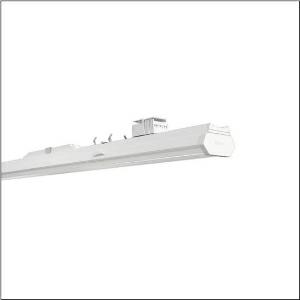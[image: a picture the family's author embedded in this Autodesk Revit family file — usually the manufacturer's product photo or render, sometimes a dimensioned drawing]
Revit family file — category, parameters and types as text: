
# Revit family: licross_r__21_protected_mo_52td12dn4a5g3s4_b622
name_source: partatom
category: Lighting Fixtures
units: mm (PartAtom-declared; Revit-internal decimal feet)

## family parameters
Cut with Voids When Loaded = No
Host = Face
Light Source = No
Part Type = Normal
Room Calculation Point = No
Round Connector Dimension = Use Diameter
Shared = No

## types (1)
- --- (1 x LED, 940 lm, 6.8 W, 4000K)
    Apparent Load = 7 VA
    CIE Flux Codes = 73 92 98 99 100
    Color Rendering = 80
    Color Temperature = 4000K
    Default Elevation = 1800 mm
    Description = Licross® 21 Protected MO, luminaire insert, of sheet steel, galvanised, coil coated, white, length: 1.500mm, width: 90mm, height: 103mm, LED rated luminous flux: 10.700lm, light colour: 840, control gear: DALI 2, with plug, 6-pole, with phase selection, for trunking rail, 9 or 11-core, mains connection: 220..240V, AC, 50/60Hz, rated input power: 66W, for trunking rail, 9-/11-core, internal wiring halogen-free, for emergency light function, converter,control gear: single battery element, battery: LiFePO4, 9Ah, primary light control with lens, of plastic, primary optical cover: cover, of PMMA, light emission: direct distribution, primary light characteristic: symmetric, protection rating (complete): IP54, insulation class (complete): insulation class I (protective earthing), certification: CE, UKCA, protection symbol: D if used in an environment with non-conductive dust loads with corresponding accessories, impact resistance: IK06, permissible ambient temperature for indoor applications: +5..+35°C, standard: EN 60598-2-22, LABS conformity tested according to VDMA 24364:2018-05, reducing of maximum allowable ambient temperature of 5°C with ceiling mounting, corresponds to IFS (International Featured Standards) requirements for safety and quality in the food industry, packaging unit: 1 piece
    Height = 92 mm
    Lamp = 1 x LED
    Lamp Light Flux = 940 lm
    Lamp Power = 6.8 W
    Lamp count = 1
    Length = 1500 mm
    Luminous efficacy = 138 lm/W
    Manufacturer = Siteco
    ModVariant = No
    Model = 52TD12DN4A5G3S4
    Mounting Place = Ceiling
    Mounting Type = Pendant
    Number of Poles = 1
    OnlyDefault = Yes
    Power Factor = 1
    Product Name = Licross® 21 Protected MO
    Product group = luminaire insert | ceiling pendant
    ProductGroupID = 902
    Protection Class = Protection class I
    Protection Degree = IP 54
    RLX_Detail_Level = 1
    RLX_Emergency_Light_Flux = 0 lm
    RLX_Emergency_Type = 0
    RLX_Emergency_Type_DB = No
    RlxData = <blob elided: 24977 chars, md5=39013eac>
    Socket = socket
    Standby Power = 0 W
    System Light Flux = 940 lm
    System Power = 7 W
    Type Comments = : emergency light operation: 3 h
    Type Image = l_1256148.jpg
    URL = http://relux.com
    VarID = @adj_132405
    Voltage = 0 V
    Weight = 0.00 kg
    Width = 88 mm

## geometry (parser evidence)
native form markers: Blend x4, Sweep x11
no freeform markers — native parametric forms only
